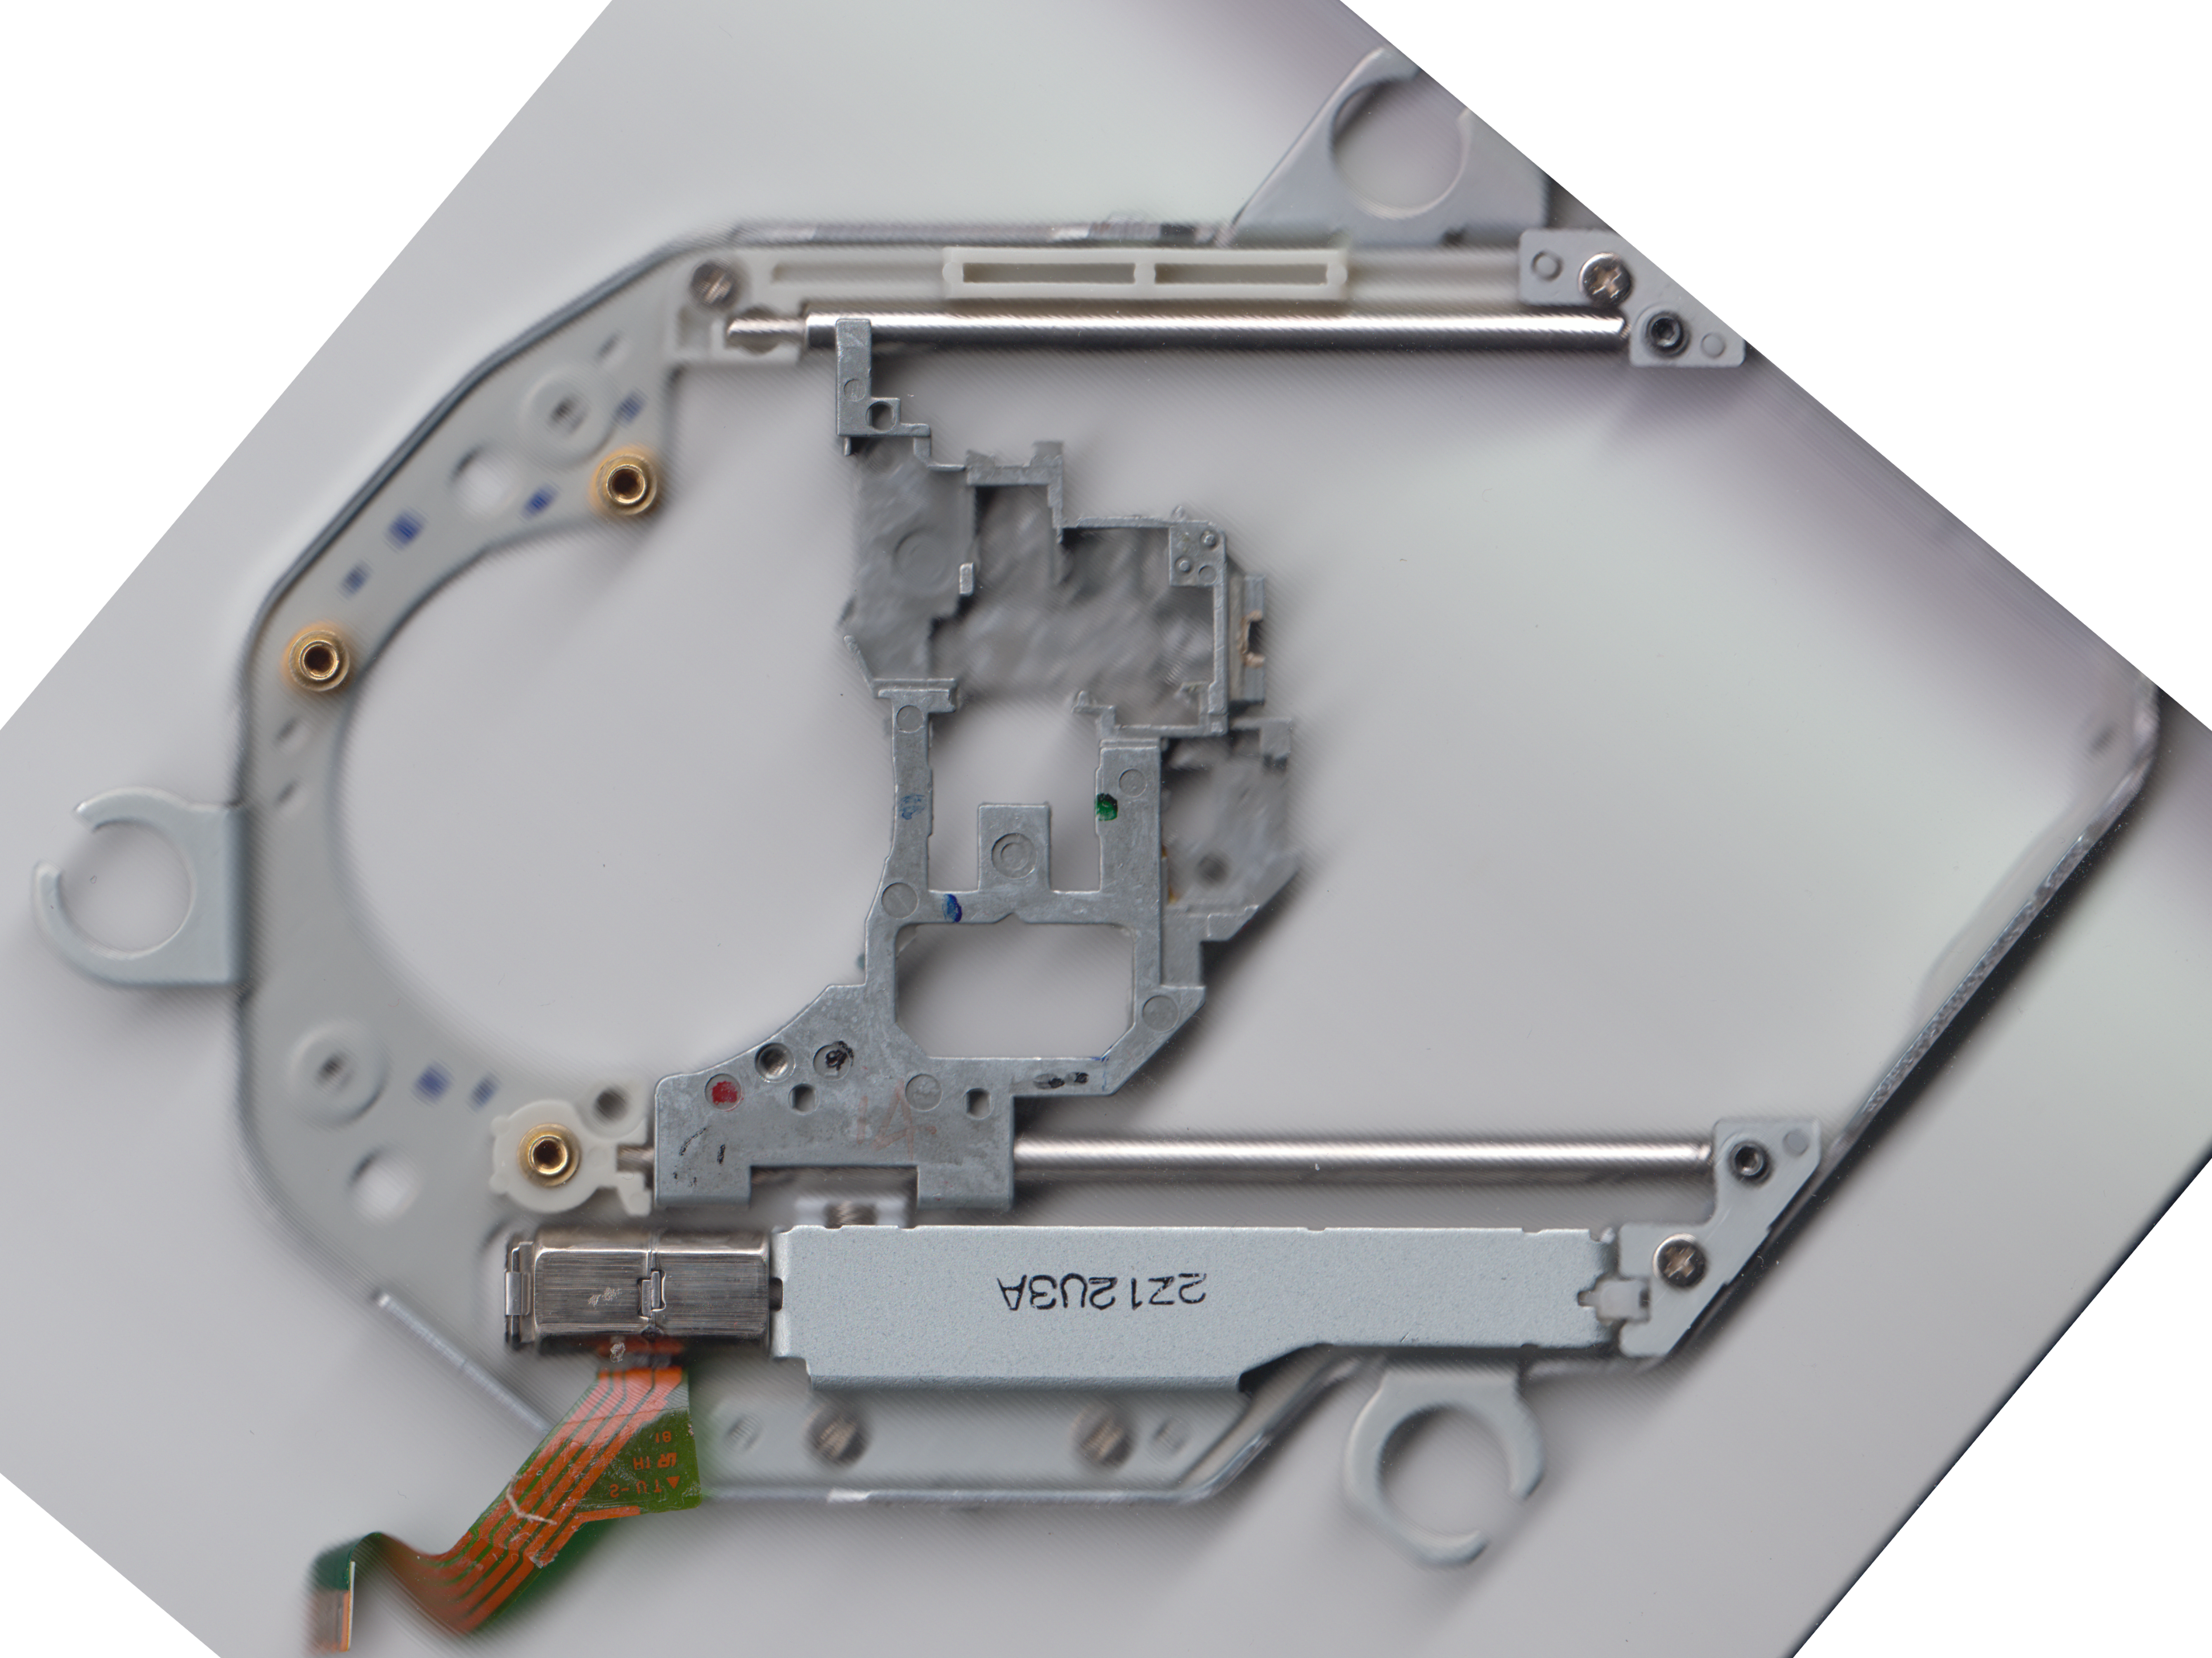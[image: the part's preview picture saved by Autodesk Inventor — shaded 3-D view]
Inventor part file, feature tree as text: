
AUTODESK INVENTOR PART (.ipt)
format: ipt  version: 2021 (Build 250183000, 183)  size: 8,595,456 bytes
history: native  units: mm
features: extrude x4, fillet x2, reference x1, imported_body x1, other x1
ambient origin geometry x8: Origin, YZ Plane, XZ Plane, XY Plane, X Axis, Y Axis, Z Axis, Center Point
bodies: Body1 (feature_tree)
feature tree (9):
  reference  "reference"
  imported_body  "base"
  extrude  "base_main"  Depth=30.0mm
  extrude  "mounting_hole_block"  Depth=7.1mm
  extrude  "mounting_hole_plate"  Depth=7.1mm
  extrude  "braass_hole"  Depth=7.1mm
  fillet  "Fillet12"  Radius=1.6mm
  fillet  "Fillet13"  Radius=1.6mm
  other  "Image2"
